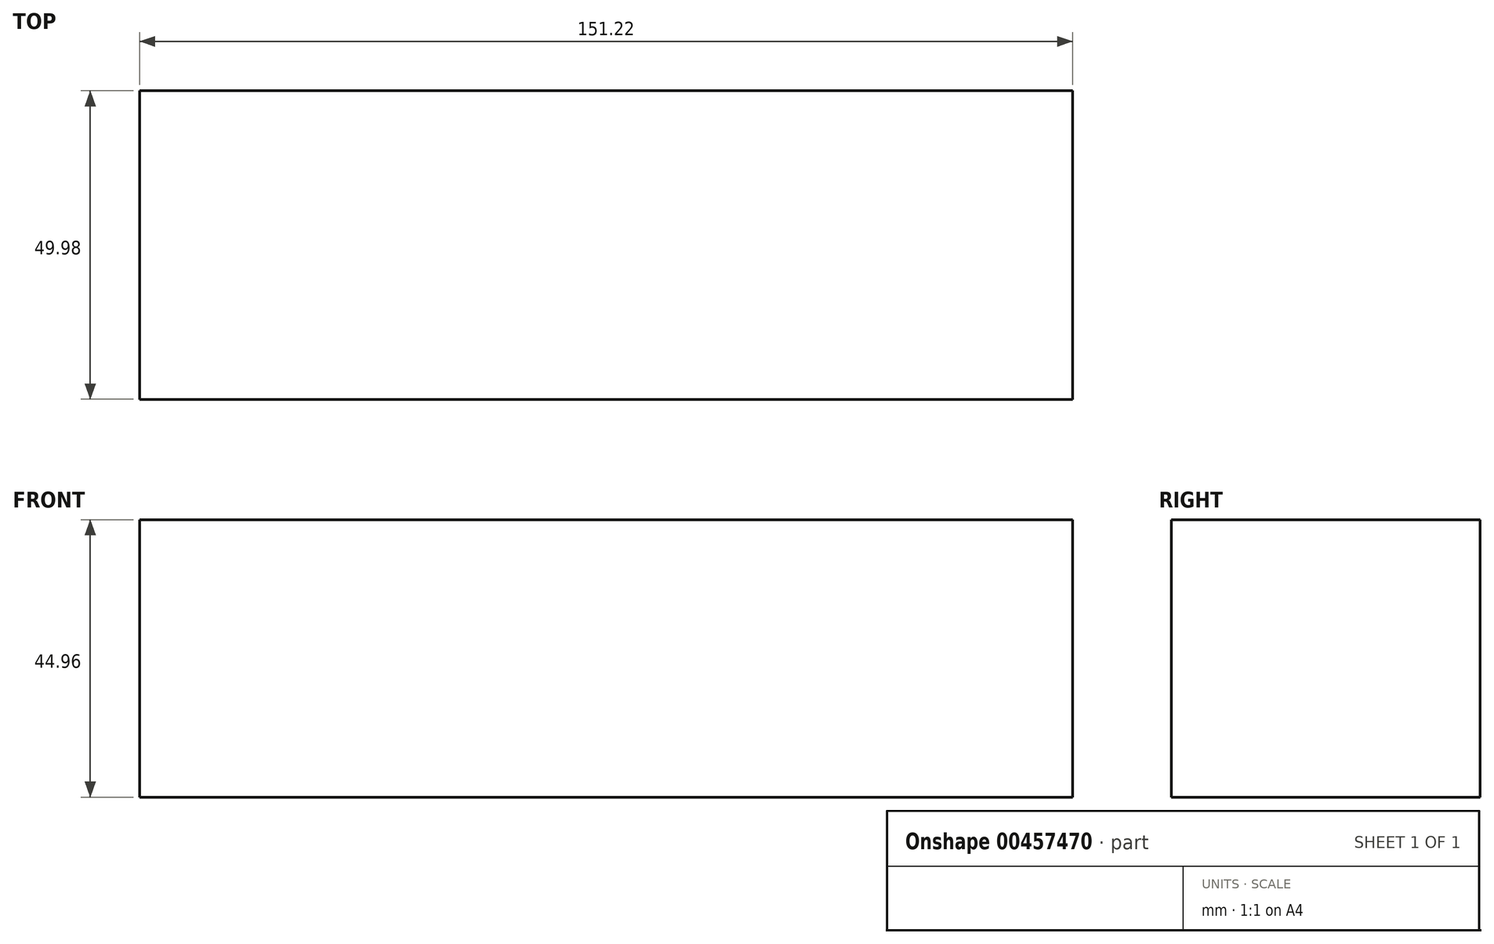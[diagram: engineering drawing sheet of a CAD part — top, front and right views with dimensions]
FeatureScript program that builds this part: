
annotation { "Feature Type Name" : "Feature", "Feature Type Description" : "" }
export const myFeature = defineFeature(function(context is Context, id is Id, definition is map)
    precondition{}
    {
        {
            var Q0;
            Q0=qCreatedBy(makeId("Top.planeOp"),FACE);
            var sketch = newSketch(context, id + "F0", { "sketchPlane" : qUnion([Q0])});
            skLineSegment(sketch, "E0.bottom", {"start": v(-75.61, -25) * mm, "end": v(75.61, -25) * mm});
            skLineSegment(sketch, "E0.top", {"start": v(-75.61, 25) * mm, "end": v(75.61, 25) * mm});
            skLineSegment(sketch, "E0.left", {"start": v(-75.61, -25) * mm, "end": v(-75.61, 25) * mm});
            skLineSegment(sketch, "E0.right", {"start": v(75.61, -25) * mm, "end": v(75.61, 25) * mm});
            skPoint(sketch, "E0.middle", {"position": v(0, 0) * mm});
            skSolve(sketch);
        }
        {
            var Q0;
            Q0 = qSketchRegion(id + "F0", true);
            extrude(context, id + "F1", {"entities" : qUnion([Q0]), "depth" : 44.96 * mm});
        }
    });
